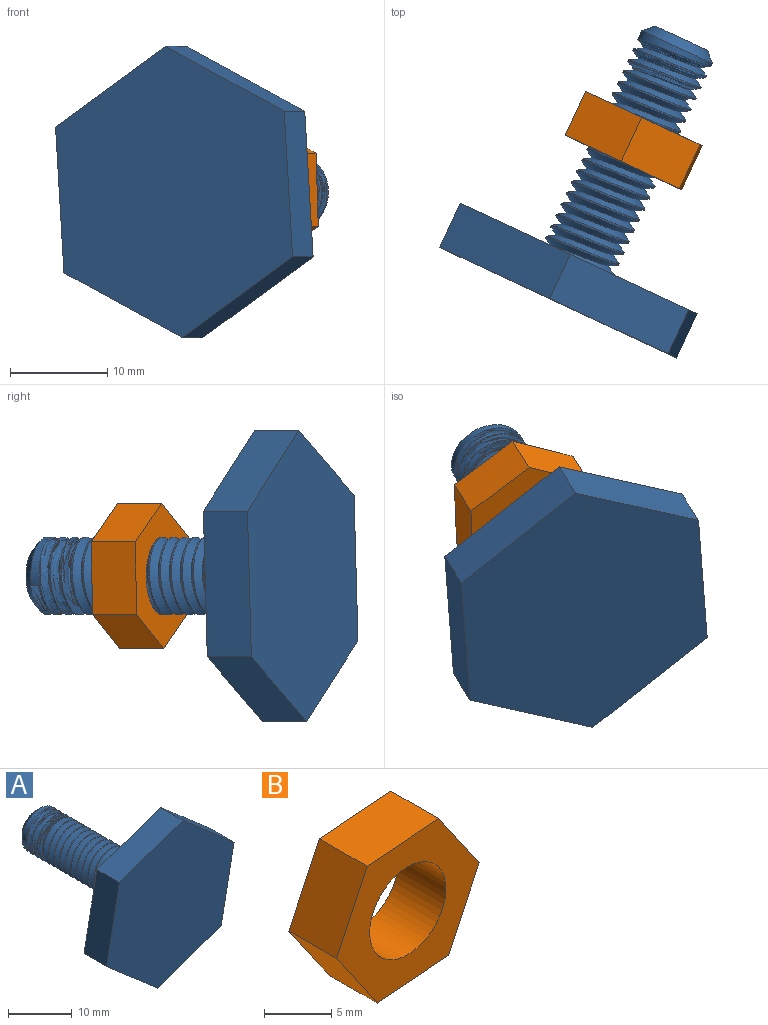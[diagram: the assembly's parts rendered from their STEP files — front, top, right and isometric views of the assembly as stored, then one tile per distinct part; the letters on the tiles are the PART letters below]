
ASSEMBLY  parts=2 mates=1
PART A: 16 faces, bbox 28.4x30x29.5 mm
  f0: cylinder r=4mm len=24mm, axis (0,1,0), area 126.2mm2, adj f9,f12,f13,f14,f15
  f1: plane 6x6mm, normal (0,1,0), area 28.3mm2, adj f15
  f2: plane 14.19x5mm, normal (-0.33,0,0.95), area 75.1mm2, adj f3,f7,f8,f9
  f3: plane 14.74x5mm, normal (-0.98,0,0.19), area 75.1mm2, adj f2,f4,f8,f9
  f4: plane 11.34x9.84mm, normal (-0.66,0,-0.76), area 75.1mm2, adj f3,f5,f8,f9
  f5: plane 14.19x5mm, normal (0.33,0,-0.95), area 75.1mm2, adj f4,f6,f8,f9
  f6: plane 14.74x5mm, normal (0.98,0,-0.19), area 75.1mm2, adj f5,f7,f8,f9
  f7: plane 11.34x9.84mm, normal (0.66,0,0.76), area 75.1mm2, adj f2,f6,f8,f9
  f8: plane 29.47x28.38mm, normal (0,-1,0), area 585.4mm2, adj f2,f3,f4,f5,f6,f7
  f9: plane 29.47x28.38mm, normal (0,1,0), area 535.2mm2, adj f0,f2,f3,f4,f5,f6,f7,f10
  f10: cylinder r=4mm len=8mm, axis (0,1,0), area 29.1mm2, adj f9,f11,f13,f14
  f11: plane 1.09x0.94mm, normal (0,0,1), area 0.5mm2, adj f10,f13,f14
  f12: plane 1.01x0.94mm, normal (0,0,-1), area 0.5mm2, adj f0,f13,f14,f15
  f13: bspline ~25.54x9.24mm, area 484.3mm2, adj f0,f10,f11,f12,f14,f15
  f14: bspline ~25.54x9.24mm, area 480mm2, adj f0,f10,f11,f12,f13
  f15: cone r=4mm half-angle=45deg, axis (0,-1,0), area 30.7mm2, adj f0,f1,f12,f13
PART B: 9 faces, bbox 15x5x13.6 mm
  f0: plane 6.78x5mm, normal (0.9,0,-0.43), area 37.5mm2, adj f1,f5,f6,f7
  f1: plane 6.18x5mm, normal (0.82,0,0.57), area 37.5mm2, adj f0,f2,f6,f7
  f2: plane 7.48x5mm, normal (-0.08,0,1), area 37.5mm2, adj f1,f3,f6,f7
  f3: plane 6.78x5mm, normal (-0.9,0,0.43), area 37.5mm2, adj f2,f4,f6,f7
  f4: plane 6.18x5mm, normal (-0.82,0,-0.57), area 37.5mm2, adj f3,f5,f6,f7
  f5: plane 7.48x5mm, normal (0.08,0,-1), area 37.5mm2, adj f0,f4,f6,f7
  f6: plane 14.96x13.57mm, normal (0,-1,0), area 96.1mm2, adj f0,f1,f2,f3,f4,f5,f8
  f7: plane 14.96x13.57mm, normal (0,1,0), area 96.1mm2, adj f0,f1,f2,f3,f4,f5,f8
  f8: cylinder r=4mm len=8mm, axis (0,-1,0), area 125.7mm2, adj f6,f7
PLACE A rot(axis=(-0.11,-0.5,-0.86),28.9deg) t=(-52.99,27.93,33.72)mm
PLACE B rot(axis=(0.22,0.97,-0.05),153.4deg) t=(-99.92,39.77,71.83)mm
MATE cylindrical A.f0 <-> B.f8  axis (0.42,0.91,0) through (-58.49,16.15,33.72)mm
